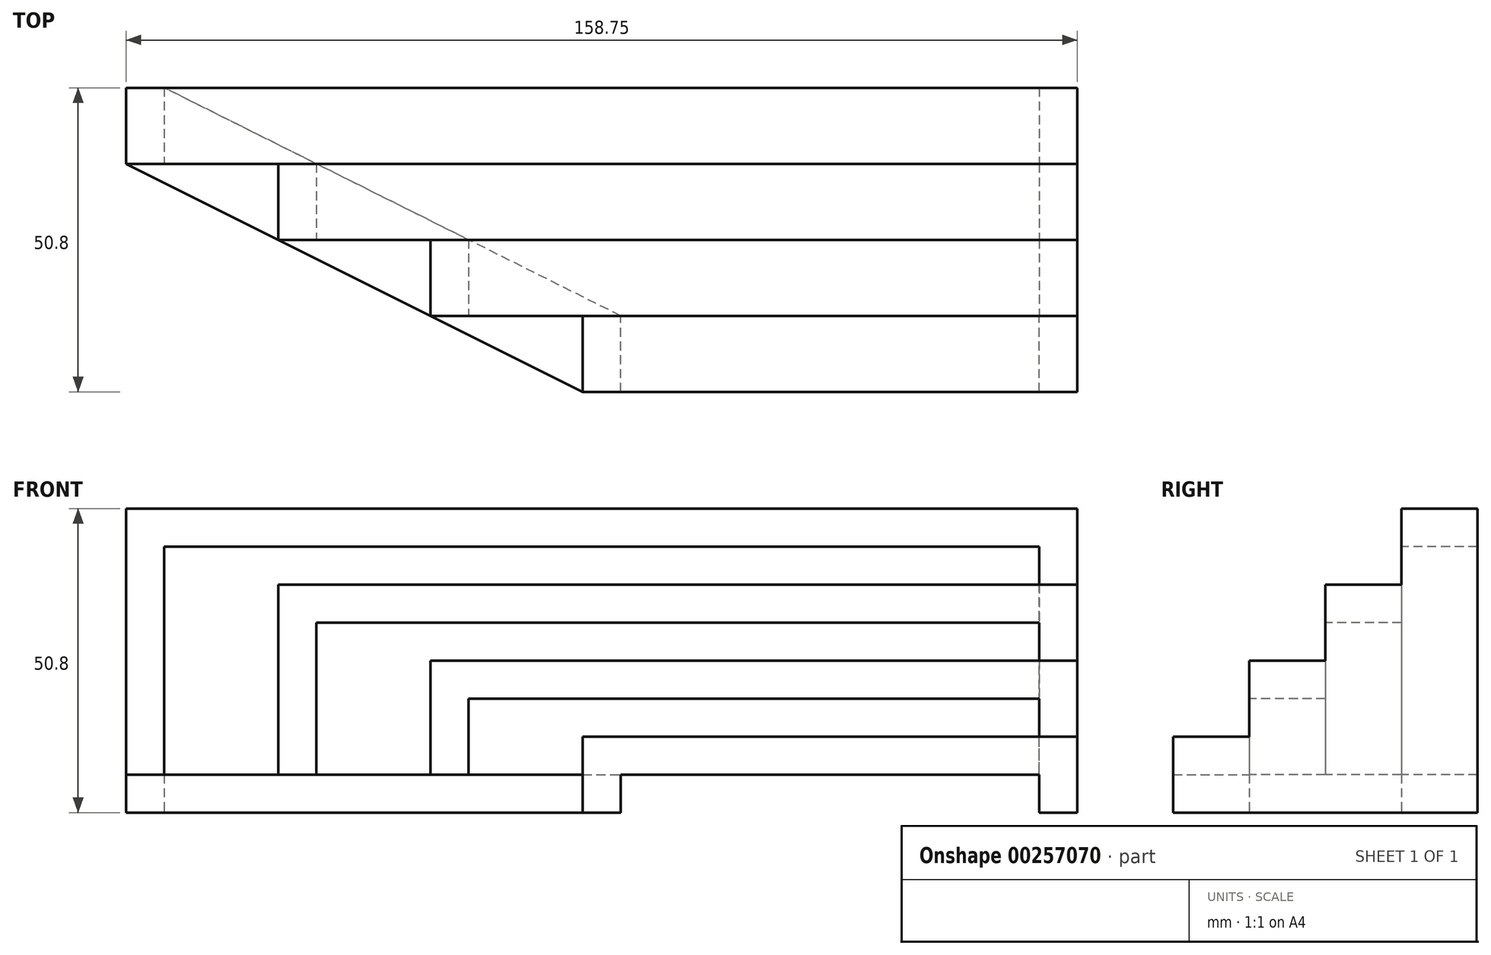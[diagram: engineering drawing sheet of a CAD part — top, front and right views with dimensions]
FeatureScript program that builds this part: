
annotation { "Feature Type Name" : "Feature", "Feature Type Description" : "" }
export const myFeature = defineFeature(function(context is Context, id is Id, definition is map)
    precondition{}
    {
        {
            var Q0;
            Q0=qCreatedBy(makeId("Front.planeOp"),FACE);
            var sketch = newSketch(context, id + "F0", { "sketchPlane" : qUnion([Q0])});
            skLineSegment(sketch, "E0", {"start": v(0, 0) * mm, "end": v(-76.2, 0) * mm});
            skLineSegment(sketch, "E1", {"start": v(-76.2, 0) * mm, "end": v(-76.2, -12.7) * mm});
            skLineSegment(sketch, "E2.0", {"start": v(-69.85, -6.35) * mm, "end": v(-69.85, -12.7) * mm});
            skLineSegment(sketch, "E2.1", {"start": v(0, -6.35) * mm, "end": v(-69.85, -6.35) * mm});
            skLineSegment(sketch, "E3", {"start": v(-76.2, -12.7) * mm, "end": v(-69.85, -12.7) * mm});
            skLineSegment(sketch, "E4", {"start": v(0, -6.35) * mm, "end": v(0, 0) * mm});
            skSolve(sketch);
        }
        {
            var Q0;
            Q0=makeQuery(id+"F0.imprint","IMPRINT",FACE,{"disambiguationData":[TD([[makeQuery(id+"F0.imprint","IMPRINT",EDGE,{"derivedFrom":sQuery(id+"F0.wireOp",EDGE,"E0")}),1.0]])]});
            extrude(context, id + "F1", {"entities" : qUnion([Q0]), "endBound" : BoundingType.SYMMETRIC, "depth" : 12.7 * mm});
        }
        {
            var Q0;
            Q0=makeQuery(id+"F1.opExtrude","CAP_FACE",FACE,{"disambiguationData":[OSD([sQuery(id+"F0.wireOp",EDGE,"E0"),sQuery(id+"F0.wireOp",EDGE,"E1"),sQuery(id+"F0.wireOp",EDGE,"E2.0"),sQuery(id+"F0.wireOp",EDGE,"E2.1"),sQuery(id+"F0.wireOp",EDGE,"E3"),sQuery(id+"F0.wireOp",EDGE,"E4")])],"isStart":true});
            var sketch = newSketch(context, id + "F2", { "sketchPlane" : qUnion([Q0])});
            skLineSegment(sketch, "E5", {"start": v(0, 12.7) * mm, "end": v(101.6, 12.7) * mm});
            skLineSegment(sketch, "E6", {"start": v(101.6, 12.7) * mm, "end": v(101.6, -12.7) * mm});
            skLineSegment(sketch, "E7.0", {"start": v(95.25, 6.35) * mm, "end": v(95.25, -12.7) * mm});
            skLineSegment(sketch, "E7.1", {"start": v(0, 6.35) * mm, "end": v(95.25, 6.35) * mm});
            skLineSegment(sketch, "E8", {"start": v(0, 12.7) * mm, "end": v(0, 6.35) * mm});
            skLineSegment(sketch, "E9", {"start": v(95.25, -12.7) * mm, "end": v(101.6, -12.7) * mm});
            skSolve(sketch);
        }
        {
            var Q0;
            Q0=makeQuery(id+"F2.imprint","IMPRINT",FACE,{"disambiguationData":[TD([[makeQuery(id+"F2.imprint","IMPRINT",EDGE,{"derivedFrom":sQuery(id+"F2.wireOp",EDGE,"E5")}),-1.0]])]});
            extrude(context, id + "F3", {"entities" : qUnion([Q0]), "depth" : 12.7 * mm});
        }
        {
            var Q0;
            Q0=makeQuery(id+"F3.opExtrude","CAP_FACE",FACE,{"disambiguationData":[OSD([sQuery(id+"F2.wireOp",EDGE,"E5"),sQuery(id+"F2.wireOp",EDGE,"E6"),sQuery(id+"F2.wireOp",EDGE,"E7.0"),sQuery(id+"F2.wireOp",EDGE,"E7.1"),sQuery(id+"F2.wireOp",EDGE,"E8"),sQuery(id+"F2.wireOp",EDGE,"E9")])],"isStart":false});
            var sketch = newSketch(context, id + "F4", { "sketchPlane" : qUnion([Q0])});
            skLineSegment(sketch, "E10", {"start": v(0, 25.4) * mm, "end": v(127, 25.4) * mm});
            skLineSegment(sketch, "E11", {"start": v(127, 25.4) * mm, "end": v(127, -12.7) * mm});
            skLineSegment(sketch, "E12.0", {"start": v(120.65, 19.05) * mm, "end": v(120.65, -12.7) * mm});
            skLineSegment(sketch, "E12.1", {"start": v(0, 19.05) * mm, "end": v(120.65, 19.05) * mm});
            skLineSegment(sketch, "E13", {"start": v(0, 25.4) * mm, "end": v(0, 19.05) * mm});
            skLineSegment(sketch, "E14", {"start": v(120.65, -12.7) * mm, "end": v(127, -12.7) * mm});
            skSolve(sketch);
        }
        {
            var Q0;
            Q0=makeQuery(id+"F4.imprint","IMPRINT",FACE,{"disambiguationData":[TD([[makeQuery(id+"F4.imprint","IMPRINT",EDGE,{"derivedFrom":sQuery(id+"F4.wireOp",EDGE,"E10")}),-1.0]])]});
            extrude(context, id + "F5", {"entities" : qUnion([Q0]), "depth" : 12.7 * mm});
        }
        {
            var Q0;
            Q0=makeQuery(id+"F5.opExtrude","CAP_FACE",FACE,{"disambiguationData":[OSD([sQuery(id+"F4.wireOp",EDGE,"E10"),sQuery(id+"F4.wireOp",EDGE,"E11"),sQuery(id+"F4.wireOp",EDGE,"E12.0"),sQuery(id+"F4.wireOp",EDGE,"E12.1"),sQuery(id+"F4.wireOp",EDGE,"E13"),sQuery(id+"F4.wireOp",EDGE,"E14")])],"isStart":false});
            var sketch = newSketch(context, id + "F6", { "sketchPlane" : qUnion([Q0])});
            skLineSegment(sketch, "E15", {"start": v(0, 38.1) * mm, "end": v(152.4, 38.1) * mm});
            skLineSegment(sketch, "E16", {"start": v(152.4, 38.1) * mm, "end": v(152.4, -12.7) * mm});
            skLineSegment(sketch, "E17.0", {"start": v(146.05, 31.75) * mm, "end": v(146.05, -12.7) * mm});
            skLineSegment(sketch, "E17.1", {"start": v(0, 31.75) * mm, "end": v(146.05, 31.75) * mm});
            skLineSegment(sketch, "E18", {"start": v(0, 38.1) * mm, "end": v(0, 31.75) * mm});
            skLineSegment(sketch, "E19", {"start": v(146.05, -12.7) * mm, "end": v(152.4, -12.7) * mm});
            skSolve(sketch);
        }
        {
            var Q0;
            Q0=makeQuery(id+"F6.imprint","IMPRINT",FACE,{"disambiguationData":[TD([[makeQuery(id+"F6.imprint","IMPRINT",EDGE,{"derivedFrom":sQuery(id+"F6.wireOp",EDGE,"E15")}),-1.0]])]});
            extrude(context, id + "F7", {"entities" : qUnion([Q0]), "depth" : 12.7 * mm});
        }
        {
            var Q0;
            Q0=qCreatedBy(makeId("Right.planeOp"),FACE);
            var sketch = newSketch(context, id + "F8", { "sketchPlane" : qUnion([Q0])});
            skLineSegment(sketch, "E20.0.2", {"start": v(44.45, -12.7) * mm, "end": v(44.45, 38.1) * mm});
            skLineSegment(sketch, "E20.0.3", {"start": v(44.45, 38.1) * mm, "end": v(31.75, 38.1) * mm});
            skLineSegment(sketch, "E20.1.2", {"start": v(-6.35, 0) * mm, "end": v(-6.35, -12.7) * mm});
            skLineSegment(sketch, "E21.1", {"start": v(31.75, 25.4) * mm, "end": v(19.05, 25.4) * mm});
            skLineSegment(sketch, "E21.2", {"start": v(19.05, 12.7) * mm, "end": v(6.35, 12.7) * mm});
            skLineSegment(sketch, "E22", {"start": v(6.35, 0) * mm, "end": v(6.35, 12.7) * mm});
            skLineSegment(sketch, "E23", {"start": v(19.05, 25.4) * mm, "end": v(19.05, 12.7) * mm});
            skLineSegment(sketch, "E24", {"start": v(31.75, 25.4) * mm, "end": v(31.75, 38.1) * mm});
            skLineSegment(sketch, "E25", {"start": v(-6.35, 0) * mm, "end": v(6.35, 0) * mm});
            skLineSegment(sketch, "E26", {"start": v(44.45, -12.7) * mm, "end": v(-6.35, -12.7) * mm});
            skSolve(sketch);
        }
        {
            var Q0;
            Q0=makeQuery(id+"F8.imprint","IMPRINT",FACE,{"disambiguationData":[TD([[makeQuery(id+"F8.imprint","IMPRINT",EDGE,{"derivedFrom":sQuery(id+"F8.wireOp",EDGE,"E20.0.2")}),1.0]])]});
            extrude(context, id + "F9", {"entities" : qUnion([Q0]), "operationType" : NewBodyOperationType.ADD, "depth" : 6.35 * mm});
        }
        {
            var Q0;
            Q0=makeQuery(id+"F1.opExtrude","SWEPT_FACE",FACE,{"disambiguationData":[OSD([sQuery(id+"F0.wireOp",EDGE,"E3")])]});
            var sketch = newSketch(context, id + "F10", { "sketchPlane" : qUnion([Q0])});
            skLineSegment(sketch, "E27.0", {"start": v(-152.4, -44.45) * mm, "end": v(-152.4, -31.75) * mm});
            skLineSegment(sketch, "E27.1", {"start": v(-76.2, 6.35) * mm, "end": v(-69.85, 6.35) * mm});
            skLineSegment(sketch, "E27.2", {"start": v(-69.85, 6.35) * mm, "end": v(-69.85, -6.35) * mm});
            skLineSegment(sketch, "E27.3", {"start": v(-146.05, -44.45) * mm, "end": v(-152.4, -44.45) * mm});
            skLineSegment(sketch, "E28", {"start": v(-152.4, -31.75) * mm, "end": v(-76.2, 6.35) * mm});
            skLineSegment(sketch, "E29", {"start": v(-69.85, -6.35) * mm, "end": v(-146.05, -44.45) * mm});
            skSolve(sketch);
        }
        {
            var Q0;
            Q0 = qSketchRegion(id + "F10", true);
            extrude(context, id + "F11", {"entities" : qUnion([Q0]), "operationType" : NewBodyOperationType.ADD, "oppositeDirection" : true, "depth" : 6.35 * mm});
        }
    });
